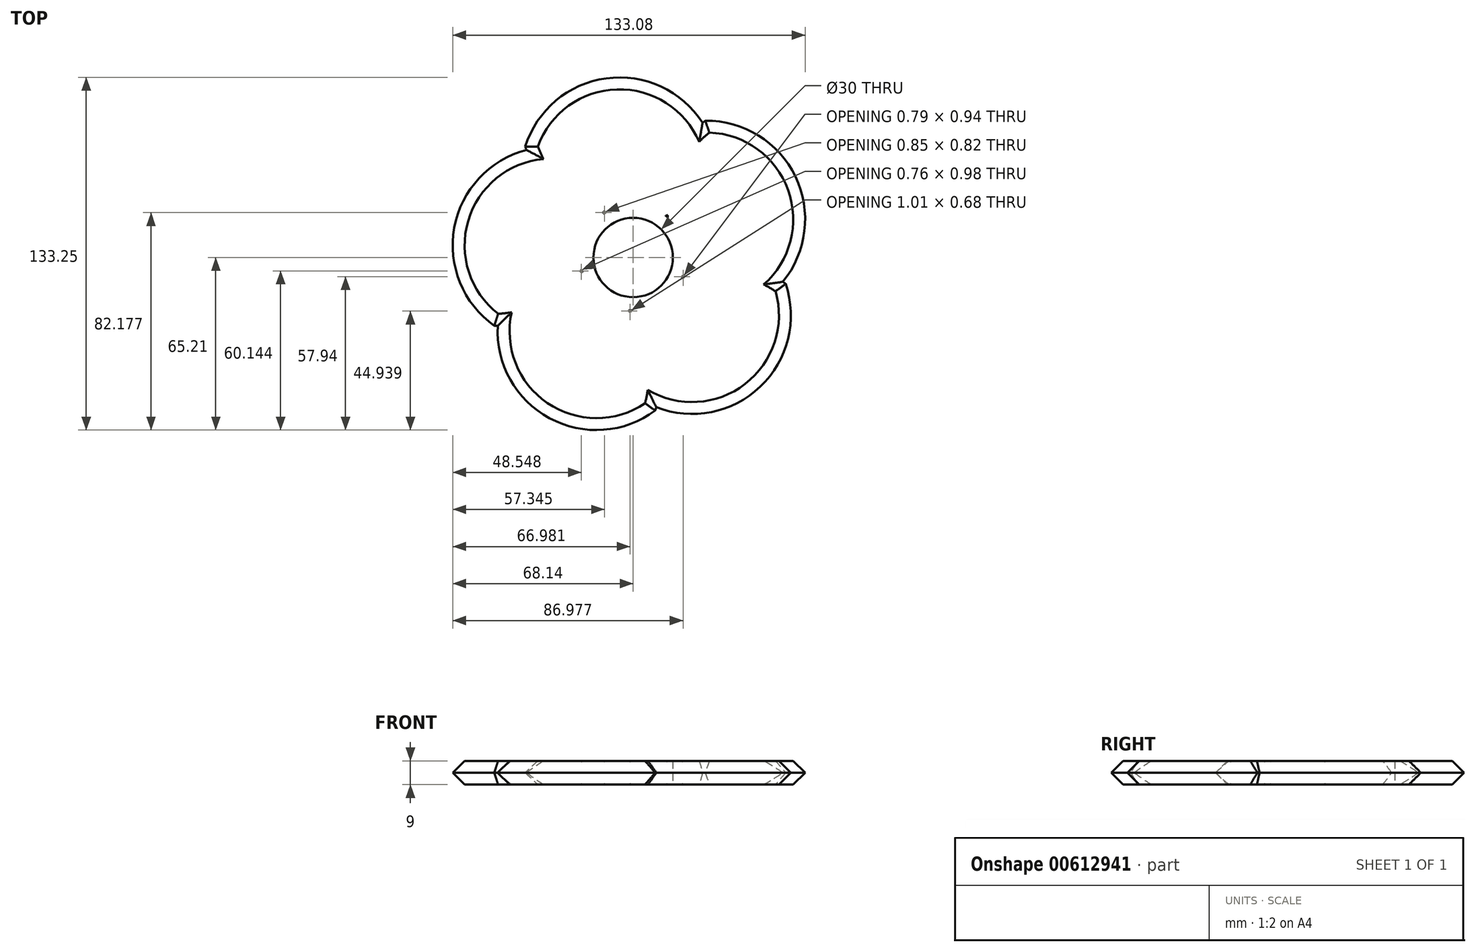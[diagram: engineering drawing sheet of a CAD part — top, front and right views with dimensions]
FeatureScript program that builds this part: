
annotation { "Feature Type Name" : "Feature", "Feature Type Description" : "" }
export const myFeature = defineFeature(function(context is Context, id is Id, definition is map)
    precondition{}
    {
        {
            var Q0;
            Q0=qCreatedBy(makeId("Top.planeOp"),FACE);
            var sketch = newSketch(context, id + "F0", { "sketchPlane" : qUnion([Q0])});
            skCircle(sketch, "E0", {"center": v(0, 0) * mm, "radius": 15 * mm});
            skCircle(sketch, "E1", {"center": v(0, 0) * mm, "radius": 20 * mm});
            skSolve(sketch);
        }
        {
            var Q0;
            Q0=makeQuery(id+"F0.imprint","IMPRINT",FACE,{"disambiguationData":[TD([[makeQuery(id+"F0.imprint","IMPRINT",EDGE,{"derivedFrom":sQuery(id+"F0.wireOp",EDGE,"E0")}),-1.0]])]});
            extrude(context, id + "F1", {"entities" : qUnion([Q0]), "depth" : 9 * mm, "offsetDistance" : 25 * mm});
        }
        {
            var Q0;
            Q0=makeQuery(id+"F1.opExtrude","CAP_FACE",FACE,{"disambiguationData":[OSD([sQuery(id+"F0.wireOp",EDGE,"E0"),sQuery(id+"F0.wireOp",EDGE,"E1")])],"isStart":true});
            var sketch = newSketch(context, id + "F2", { "sketchPlane" : qUnion([Q0])});
            skCircle(sketch, "E2", {"center": v(27.66, -14.43) * mm, "radius": 37.78 * mm});
            skCircle(sketch, "E3", {"center": v(55.08, -14.43) * mm, "radius": 47.02 * mm});
            skSolve(sketch);
        }
        {
            var Q0;
            {var subQ0=sQuery(id+"F2.wireOp",EDGE,"E3");var subQ1=sQuery(id+"F2.wireOp",EDGE,"E2");var subQ2=makeQuery(id+"F2.imprint","INTERSECT",VERTEX,{"disambiguationData":[OD(1.0)],"derivedFrom":[subQ1,subQ0]});Q0=makeQuery(id+"F2.imprint","IMPRINT",FACE,{"disambiguationData":[TD([[makeQuery(id+"F2.imprint","IMPRINT",EDGE,{"disambiguationData":[TD([[subQ2,1.0]])],"derivedFrom":subQ1}),1.0]])]});}
            extrude(context, id + "F3", {"entities" : qUnion([Q0]), "operationType" : NewBodyOperationType.ADD, "oppositeDirection" : true, "depth" : 9 * mm, "offsetDistance" : 25 * mm});
        }
        {
            var Q0;
            Q0=makeQuery(id+"F3.opExtrude","CAP_EDGE",EDGE,{"disambiguationData":[OSD([sQuery(id+"F2.wireOp",EDGE,"E3")])],"isStart":false});
            var Q1;
            Q1=makeQuery(id+"F3.opExtrude","CAP_EDGE",EDGE,{"disambiguationData":[OSD([sQuery(id+"F2.wireOp",EDGE,"E2")])],"isStart":false});
            chamfer(context, id + "F4", {"entities" : qUnion([Q0, Q1]), "width" : 5 * mm, "tangentPropagation" : true});
        }
        {
            var Q0;
            Q0=makeQuery(id+"F3.opExtrude","CAP_EDGE",EDGE,{"disambiguationData":[OSD([sQuery(id+"F2.wireOp",EDGE,"E2")])],"isStart":true});
            var Q1;
            Q1=makeQuery(id+"F3.opExtrude","CAP_EDGE",EDGE,{"disambiguationData":[OSD([sQuery(id+"F2.wireOp",EDGE,"E3")])],"isStart":true});
            chamfer(context, id + "F5", {"entities" : qUnion([Q0, Q1]), "width" : 5 * mm, "tangentPropagation" : true});
        }
        {
            var Q0;
            Q0=makeQuery(id+"F1.opExtrude","SWEPT_BODY",BODY,{"disambiguationData":[OSD([sQuery(id+"F0.wireOp",EDGE,"E0"),sQuery(id+"F0.wireOp",EDGE,"E1")])]});
            var Q1;
            Q1=makeQuery(id+"F1.opExtrude","SWEPT_FACE",FACE,{"disambiguationData":[OSD([sQuery(id+"F0.wireOp",EDGE,"E1")])]});
            circularPattern(context, id + "F6", {"operationType" : NewBodyOperationType.ADD, "entities" : qUnion([Q0]), "axis" : qUnion([Q1]), "angle" : 360 * degree, "instanceCount" : 5, "equalSpace" : true});
        }
    });
